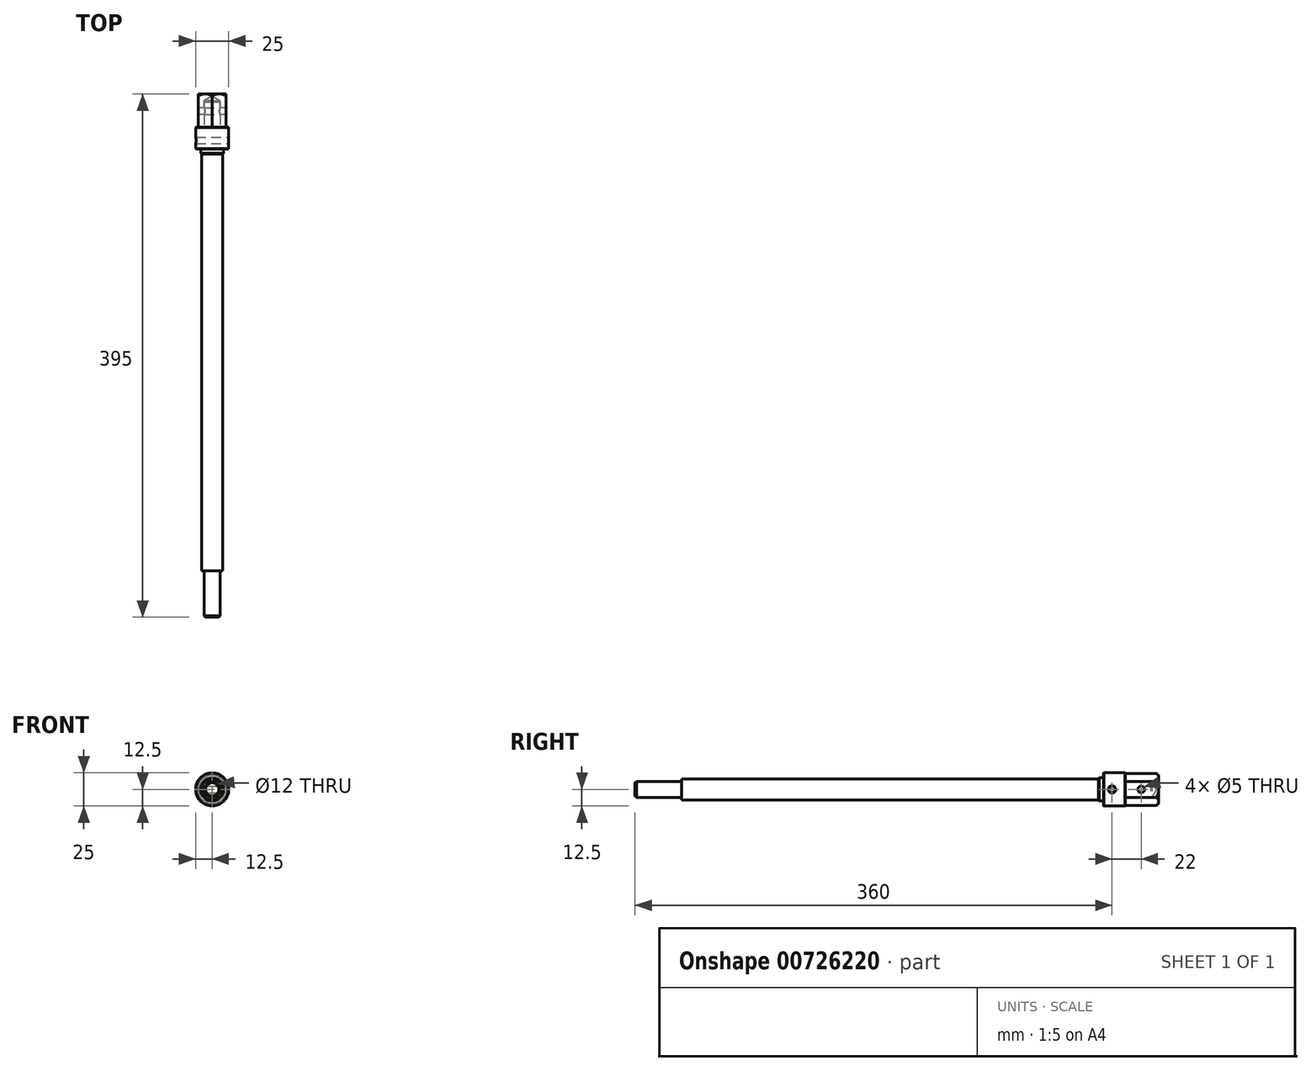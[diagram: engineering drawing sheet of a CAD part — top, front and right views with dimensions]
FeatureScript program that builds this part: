
annotation { "Feature Type Name" : "Feature", "Feature Type Description" : "" }
export const myFeature = defineFeature(function(context is Context, id is Id, definition is map)
    precondition{}
    {
        {
            var Q0;
            Q0=qCreatedBy(makeId("Front.planeOp"),FACE);
            var sketch = newSketch(context, id + "F0", { "sketchPlane" : qUnion([Q0])});
            skCircle(sketch, "E0.cCircle", {"center": v(0, 0) * mm, "radius": 10.5 * mm, "construction": true});
            skLineSegment(sketch, "E0.0", {"start": v(0, 12.12) * mm, "end": v(10.5, 6.06) * mm});
            skLineSegment(sketch, "E0.1", {"start": v(10.5, 6.06) * mm, "end": v(10.5, -6.06) * mm});
            skLineSegment(sketch, "E0.2", {"start": v(10.5, -6.06) * mm, "end": v(0, -12.12) * mm});
            skLineSegment(sketch, "E0.3", {"start": v(0, -12.12) * mm, "end": v(-10.5, -6.06) * mm});
            skLineSegment(sketch, "E0.4", {"start": v(-10.5, -6.06) * mm, "end": v(-10.5, 6.06) * mm});
            skLineSegment(sketch, "E0.5", {"start": v(-10.5, 6.06) * mm, "end": v(0, 12.12) * mm});
            skPoint(sketch, "E0.0.midPoint", {"position": v(5.25, 9.1) * mm});
            skSolve(sketch);
        }
        {
            var Q0;
            Q0=qSketchRegion(id+"F0",true);
            extrude(context, id + "F1", {"entities" : qUnion([Q0]), "depth" : 25 * mm, "offsetDistance" : 25 * mm});
        }
        {
            var Q0;
            Q0=qCreatedBy(makeId("Right.planeOp"),FACE);
            var sketch = newSketch(context, id + "F2", { "sketchPlane" : qUnion([Q0])});
            skLineSegment(sketch, "E1", {"start": v(0, 12.12) * mm, "end": v(-1.5, 12.12) * mm});
            skLineSegment(sketch, "E2", {"start": v(-1.5, 12.12) * mm, "end": v(0, 10.62) * mm});
            skLineSegment(sketch, "E3", {"start": v(0, 10.62) * mm, "end": v(0, 12.12) * mm});
            skLineSegment(sketch, "E4", {"start": v(0, 0) * mm, "end": v(-6.38, 0) * mm, "construction": true});
            skSolve(sketch);
        }
        {
            var Q0;
            Q0=qSketchRegion(id+"F2",true);
            var Q1;
            Q1=sQuery(id+"F2.wireOp",EDGE,"E4");
            revolve(context, id + "F3", {"operationType" : NewBodyOperationType.REMOVE, "entities" : qUnion([Q0]), "axis" : qUnion([Q1]), "revolveType" : RevolveType.FULL});
        }
        {
            var Q0;
            Q0=makeQuery(id+"F1.opExtrude","CAP_FACE",FACE,{"disambiguationData":[OSD([sQuery(id+"F0.wireOp",EDGE,"E0.0"),sQuery(id+"F0.wireOp",EDGE,"E0.1"),sQuery(id+"F0.wireOp",EDGE,"E0.2"),sQuery(id+"F0.wireOp",EDGE,"E0.3"),sQuery(id+"F0.wireOp",EDGE,"E0.4"),sQuery(id+"F0.wireOp",EDGE,"E0.5")])],"isStart":false});
            var sketch = newSketch(context, id + "F4", { "sketchPlane" : qUnion([Q0])});
            skPoint(sketch, "E5", {"position": v(0, 0) * mm});
            skSolve(sketch);
        }
        {
            var Q0;
            Q0=sQuery(id+"F4.wireOp",VERTEX,"E5");
            var Q1;
            Q1=makeQuery(id+"F1.opExtrude","SWEPT_BODY",BODY,{"disambiguationData":[OSD([sQuery(id+"F0.wireOp",EDGE,"E0.0"),sQuery(id+"F0.wireOp",EDGE,"E0.1"),sQuery(id+"F0.wireOp",EDGE,"E0.2"),sQuery(id+"F0.wireOp",EDGE,"E0.3"),sQuery(id+"F0.wireOp",EDGE,"E0.4"),sQuery(id+"F0.wireOp",EDGE,"E0.5")])]});
            hole(context, id + "F5", {"style" : HoleStyle.SIMPLE, "endStyle" : HoleEndStyle.BLIND, "holeDiameter" : 12 * mm, "holeDepth" : 20 * mm, "tappedDepth" : 10 * mm, "tapClearance" : 2, "locations" : qUnion([Q0]), "scope" : qUnion([Q1]), "majorDiameter" : 5 * mm, "startStyle" : HoleStartStyle.PART});
        }
        {
            var Q0;
            Q0=makeQuery(id+"F1.opExtrude","SWEPT_FACE",FACE,{"disambiguationData":[OSD([sQuery(id+"F0.wireOp",EDGE,"E0.1")])]});
            var sketch = newSketch(context, id + "F6", { "sketchPlane" : qUnion([Q0])});
            skPoint(sketch, "E6", {"position": v(-13, 0) * mm});
            skSolve(sketch);
        }
        {
            var Q0;
            Q0=sQuery(id+"F6.wireOp",VERTEX,"61b6d332-a3a9-4a86-aea2-c6c1109fe6f7");
            var Q1;
            Q1=sQuery(id+"F6.wireOp",VERTEX,"E6");
            var Q2;
            Q2=makeQuery(id+"F1.opExtrude","SWEPT_BODY",BODY,{"disambiguationData":[OSD([sQuery(id+"F0.wireOp",EDGE,"E0.0"),sQuery(id+"F0.wireOp",EDGE,"E0.1"),sQuery(id+"F0.wireOp",EDGE,"E0.2"),sQuery(id+"F0.wireOp",EDGE,"E0.3"),sQuery(id+"F0.wireOp",EDGE,"E0.4"),sQuery(id+"F0.wireOp",EDGE,"E0.5")])]});
            hole(context, id + "F7", {"style" : HoleStyle.SIMPLE, "endStyle" : HoleEndStyle.THROUGH, "standardTappedOrClearance" : lookupTablePath({ "standard" : "ISO", "size" : "5", "type" : "Drilled" }), "standardBlindInLast" : lookupTablePath({ "standard" : "ISO", "size" : "5", "type" : "Drilled" }), "holeDiameter" : 5 * mm, "tappedDepth" : 10 * mm, "tapClearance" : 2, "locations" : qUnion([Q0, Q1]), "scope" : qUnion([Q2]), "majorDiameter" : 5 * mm, "startStyle" : HoleStartStyle.PART});
        }
        {
            var Q0;
            Q0=makeQuery(id+"F1.opExtrude","CAP_FACE",FACE,{"disambiguationData":[OSD([sQuery(id+"F0.wireOp",EDGE,"E0.0"),sQuery(id+"F0.wireOp",EDGE,"E0.1"),sQuery(id+"F0.wireOp",EDGE,"E0.2"),sQuery(id+"F0.wireOp",EDGE,"E0.3"),sQuery(id+"F0.wireOp",EDGE,"E0.4"),sQuery(id+"F0.wireOp",EDGE,"E0.5")])],"isStart":false});
            var sketch = newSketch(context, id + "F8", { "sketchPlane" : qUnion([Q0])});
            skCircle(sketch, "E7", {"center": v(0, 0) * mm, "radius": 12.5 * mm});
            skCircle(sketch, "E8", {"center": v(0, 0) * mm, "radius": 6 * mm});
            skSolve(sketch);
        }
        {
            var Q0;
            Q0=qSketchRegion(id+"F8",true);
            extrude(context, id + "F9", {"entities" : qUnion([Q0]), "depth" : 20 * mm, "offsetDistance" : 25 * mm});
        }
        {
            var Q0;
            Q0=makeQuery(id+"F9.opExtrude","CAP_FACE",FACE,{"disambiguationData":[OSD([sQuery(id+"F8.wireOp",EDGE,"E7"),sQuery(id+"F8.wireOp",EDGE,"E8")])],"isStart":false});
            var sketch = newSketch(context, id + "F10", { "sketchPlane" : qUnion([Q0])});
            skCircle(sketch, "E9", {"center": v(0, 0) * mm, "radius": 6 * mm});
            skSolve(sketch);
        }
        {
            var Q0;
            Q0=qSketchRegion(id+"F10",true);
            extrude(context, id + "F11", {"entities" : qUnion([Q0]), "oppositeDirection" : true, "depth" : (54 - 15) * mm, "offsetDistance" : 25 * mm});
        }
        {
            var Q0;
            Q0=makeQuery(id+"F11.opExtrude","CAP_FACE",FACE,{"disambiguationData":[OSD([sQuery(id+"F10.wireOp",EDGE,"E9")])],"isStart":true});
            var sketch = newSketch(context, id + "F12", { "sketchPlane" : qUnion([Q0])});
            skCircle(sketch, "E10", {"center": v(0, 0) * mm, "radius": 8 * mm});
            skSolve(sketch);
        }
        {
            var Q0;
            Q0=qSketchRegion(id+"F12",true);
            extrude(context, id + "F13", {"entities" : qUnion([Q0]), "operationType" : NewBodyOperationType.ADD, "depth" : 315 * mm, "offsetDistance" : 25 * mm});
        }
        {
            var Q0;
            Q0=makeQuery(id+"F13.opExtrude","CAP_FACE",FACE,{"disambiguationData":[OSD([sQuery(id+"F12.wireOp",EDGE,"E10")])],"isStart":false});
            var sketch = newSketch(context, id + "F14", { "sketchPlane" : qUnion([Q0])});
            skCircle(sketch, "E11", {"center": v(0, 0) * mm, "radius": 6 * mm});
            skSolve(sketch);
        }
        {
            var Q0;
            Q0=qSketchRegion(id+"F14",true);
            extrude(context, id + "F15", {"entities" : qUnion([Q0]), "operationType" : NewBodyOperationType.ADD, "depth" : 35 * mm, "offsetDistance" : 25 * mm});
        }
        {
            var Q0;
            Q0=makeQuery(id+"F15.opExtrude","CAP_EDGE",EDGE,{"disambiguationData":[OSD([sQuery(id+"F14.wireOp",EDGE,"E11")])],"isStart":false});
            chamfer(context, id + "F16", {"entities" : qUnion([Q0]), "width" : 1 * mm, "tangentPropagation" : true});
        }
        {
            var Q0;
            Q0=qCreatedBy(makeId("Right.planeOp"),FACE);
            var sketch = newSketch(context, id + "F17", { "sketchPlane" : qUnion([Q0])});
            skCircle(sketch, "E12", {"center": v(-35, 0) * mm, "radius": 2.5 * mm});
            skSolve(sketch);
        }
        {
            var Q0;
            Q0=qSketchRegion(id+"F17",true);
            extrude(context, id + "F18", {"entities" : qUnion([Q0]), "operationType" : NewBodyOperationType.REMOVE, "oppositeDirection" : true, "depth" : 25 * mm, "offsetDistance" : 25 * mm, "symmetric" : true});
        }
        {
            var Q0;
            Q0=qCreatedBy(makeId("Right.planeOp"),FACE);
            var sketch = newSketch(context, id + "F19", { "sketchPlane" : qUnion([Q0])});
            skCircle(sketch, "E13", {"center": v(-35, 0) * mm, "radius": 2.5 * mm});
            skCircle(sketch, "E14", {"center": v(-13, 0) * mm, "radius": 2.5 * mm});
            skSolve(sketch);
        }
        {
            var Q0;
            Q0=qSketchRegion(id+"F19",true);
            extrude(context, id + "F20", {"entities" : qUnion([Q0]), "operationType" : NewBodyOperationType.REMOVE, "oppositeDirection" : true, "depth" : 25 * mm, "offsetDistance" : 25 * mm, "symmetric" : true});
        }
        {
            var Q0;
            Q0=makeQuery(id+"F9.opExtrude","CAP_FACE",FACE,{"disambiguationData":[OSD([sQuery(id+"F8.wireOp",EDGE,"E7"),sQuery(id+"F8.wireOp",EDGE,"E8")])],"isStart":false});
            var sketch = newSketch(context, id + "F21", { "sketchPlane" : qUnion([Q0])});
            skCircle(sketch, "E15", {"center": v(0, 0) * mm, "radius": 8.68 * mm});
            skSolve(sketch);
        }
        {
            var Q0;
            Q0=makeQuery(id+"F21.imprint","IMPRINT",FACE,{"disambiguationData":[TD([[makeQuery(id+"F21.imprint","IMPRINT",EDGE,{"derivedFrom":sQuery(id+"F21.wireOp",EDGE,"E15")}),-1.0]])]});
            extrude(context, id + "F22", {"entities" : qUnion([Q0]), "operationType" : NewBodyOperationType.REMOVE, "oppositeDirection" : true, "depth" : 3.5 * mm, "offsetDistance" : 25 * mm});
        }
        {
            var Q0;
            Q0=makeQuery(id+"F9.opExtrude","CAP_FACE",FACE,{"disambiguationData":[OSD([sQuery(id+"F8.wireOp",EDGE,"E7"),sQuery(id+"F8.wireOp",EDGE,"E8")])],"isStart":false});
            var Q1;
            Q1=makeQuery(id+"F9.opExtrude","SWEPT_FACE",FACE,{"disambiguationData":[OSD([sQuery(id+"F8.wireOp",EDGE,"E7")])]});
            chamfer(context, id + "F23", {"entities" : qUnion([Q0, Q1]), "width" : .25 * mm, "tangentPropagation" : true});
        }
    });
